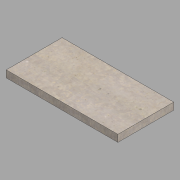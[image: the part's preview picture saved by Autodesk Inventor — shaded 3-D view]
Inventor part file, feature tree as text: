
AUTODESK INVENTOR PART (.ipt)
format: ipt  version: 2022 (Build 260153000, 153)  size: 117,760 bytes
history: native  units: in
note: dims shown in document units (in); Inventor stores cm internally (conversion verified against a paired STEP export)
features: extrude x1, sketch x1
ambient origin geometry x8: Origin, YZ Plane, XZ Plane, XY Plane, X Axis, Y Axis, Z Axis, Center Point
bodies: Solid1 (feature_tree)
feature tree (2):
  extrude  "Extrusion1"  Depth=24.0in
  sketch  "Sketch1"  dims[d0=48.0in d1=24.0in d2=3.0in d3=0.0in]
